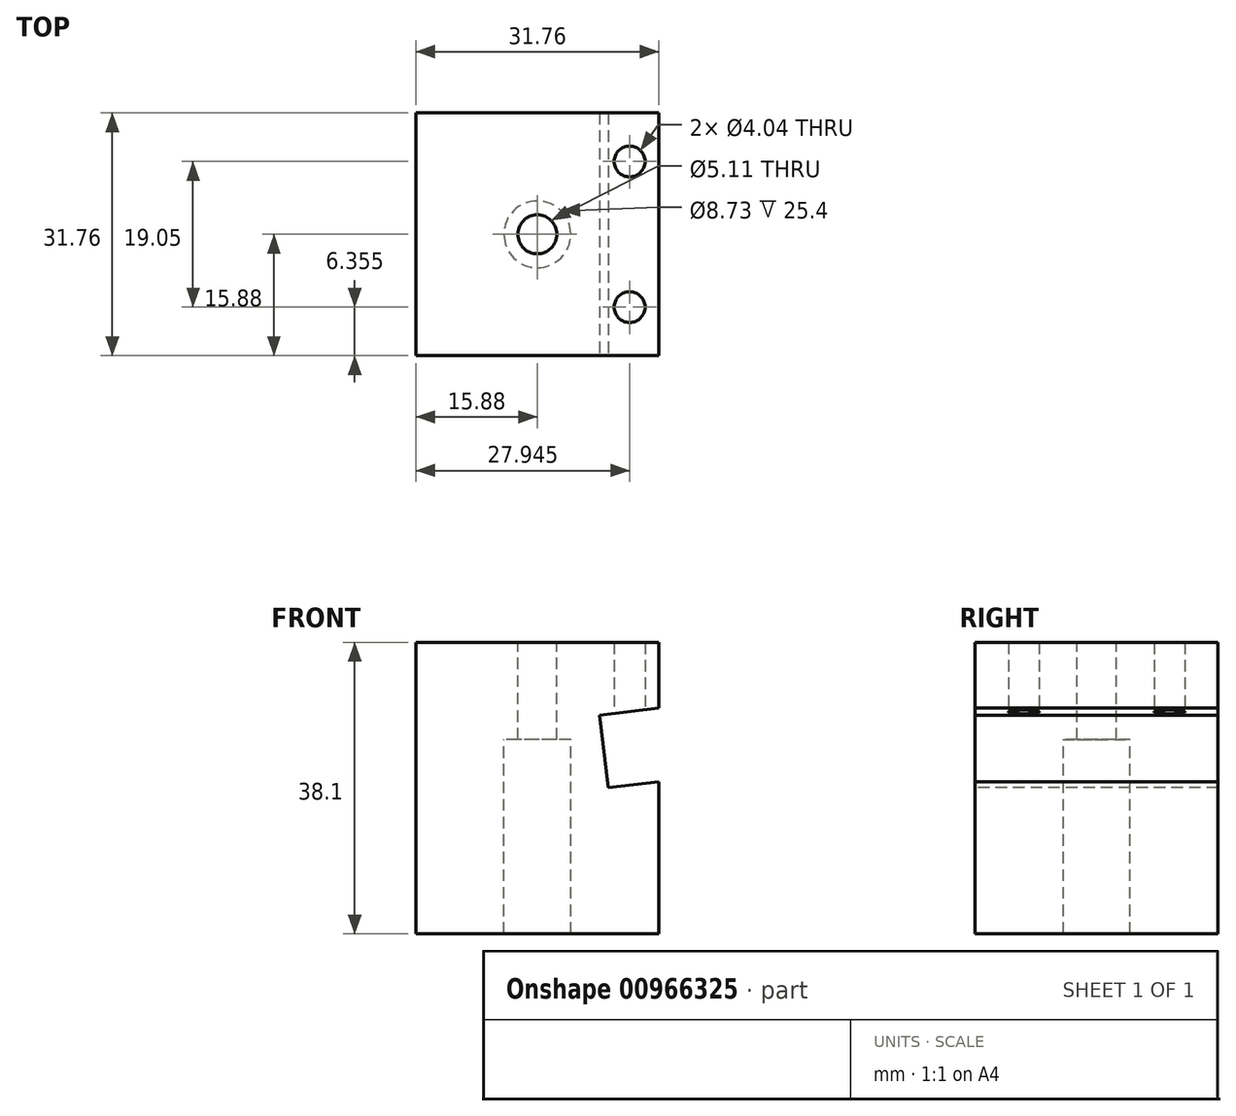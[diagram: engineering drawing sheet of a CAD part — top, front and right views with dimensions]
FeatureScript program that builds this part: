
annotation { "Feature Type Name" : "Feature", "Feature Type Description" : "" }
export const myFeature = defineFeature(function(context is Context, id is Id, definition is map)
    precondition{}
    {
        {
            var Q0;
            Q0=qCreatedBy(makeId("Top.planeOp"),FACE);
            var sketch = newSketch(context, id + "F0", { "sketchPlane" : qUnion([Q0])});
            skLineSegment(sketch, "E0.bottom", {"start": v(15.88, 15.88) * mm, "end": v(-15.88, 15.88) * mm});
            skLineSegment(sketch, "E0.top", {"start": v(15.88, -15.88) * mm, "end": v(-15.88, -15.88) * mm});
            skLineSegment(sketch, "E0.left", {"start": v(15.88, 15.88) * mm, "end": v(15.88, -15.88) * mm});
            skLineSegment(sketch, "E0.right", {"start": v(-15.88, 15.88) * mm, "end": v(-15.88, -15.88) * mm});
            skPoint(sketch, "E0.middle", {"position": v(0, 0) * mm});
            skSolve(sketch);
        }
        {
            var Q0;
            Q0=qSketchRegion(id+"F0",true);
            extrude(context, id + "F1", {"entities" : qUnion([Q0]), "depth" : 38.1 * mm, "offsetDistance" : 25.4 * mm});
        }
        {
            var Q0;
            Q0=qCreatedBy(makeId("Top.planeOp"),FACE);
            var sketch = newSketch(context, id + "F2", { "sketchPlane" : qUnion([Q0])});
            skPoint(sketch, "E1", {"position": v(0, 0) * mm});
            skSolve(sketch);
        }
        {
            var Q0;
            Q0=sQuery(id+"F2.wireOp",VERTEX,"E1");
            var Q1;
            Q1=makeQuery(id+"F1.opExtrude","SWEPT_BODY",BODY,{"disambiguationData":[OSD([sQuery(id+"F0.wireOp",EDGE,"E0.bottom"),sQuery(id+"F0.wireOp",EDGE,"E0.top"),sQuery(id+"F0.wireOp",EDGE,"E0.left"),sQuery(id+"F0.wireOp",EDGE,"E0.right")])]});
            hole(context, id + "F3", {"style" : HoleStyle.C_BORE, "endStyle" : HoleEndStyle.THROUGH, "oppositeDirection" : true, "standardTappedOrClearance" : lookupTablePath({ "standard" : "ANSI", "size" : "#7 (0.2)", "type" : "Drilled" }), "standardBlindInLast" : lookupTablePath({ "standard" : "ANSI", "size" : "#7", "type" : "Drilled" }), "holeDiameter" : 5.1 * mm, "cBoreDiameter" : 8.73 * mm, "cBoreDepth" : 25.4 * mm, "isTappedThrough" : true, "tappedDepth" : 18.42 * mm, "tapClearance" : 3, "startFromSketch" : true, "locations" : qUnion([Q0]), "scope" : qUnion([Q1])});
        }
        {
            var Q0;
            Q0=makeQuery(id+"F1.opExtrude","SWEPT_FACE",FACE,{"disambiguationData":[OSD([sQuery(id+"F0.wireOp",EDGE,"E0.top")])]});
            var sketch = newSketch(context, id + "F4", { "sketchPlane" : qUnion([Q0])});
            skLineSegment(sketch, "E2", {"start": v(33.32, 31.63) * mm, "end": v(8.11, 28.54) * mm});
            skLineSegment(sketch, "E3", {"start": v(8.11, 28.54) * mm, "end": v(9.27, 19.09) * mm});
            skLineSegment(sketch, "E4", {"start": v(9.27, 19.09) * mm, "end": v(34.48, 22.18) * mm});
            skLineSegment(sketch, "E5", {"start": v(34.48, 22.18) * mm, "end": v(33.32, 31.63) * mm});
            skLineSegment(sketch, "E6", {"start": v(8.7, 23.81) * mm, "end": v(74.38, 23.81) * mm, "construction": true});
            skSolve(sketch);
        }
        {
            var Q0;
            Q0=qSketchRegion(id+"F4",true);
            extrude(context, id + "F5", {"entities" : qUnion([Q0]), "operationType" : NewBodyOperationType.REMOVE, "endBound" : BoundingType.THROUGH_ALL, "oppositeDirection" : true, "depth" : 25.4 * mm, "offsetDistance" : 25.4 * mm});
        }
        {
            var Q0;
            Q0=makeQuery(id+"F1.opExtrude","CAP_FACE",FACE,{"disambiguationData":[OSD([sQuery(id+"F0.wireOp",EDGE,"E0.bottom"),sQuery(id+"F0.wireOp",EDGE,"E0.top"),sQuery(id+"F0.wireOp",EDGE,"E0.left"),sQuery(id+"F0.wireOp",EDGE,"E0.right")])],"isStart":false});
            var sketch = newSketch(context, id + "F6", { "sketchPlane" : qUnion([Q0])});
            skLineSegment(sketch, "E7", {"start": v(12.07, -9.53) * mm, "end": v(12.07, 9.53) * mm, "construction": true});
            skPoint(sketch, "E8", {"position": v(12.07, 9.53) * mm});
            skPoint(sketch, "E9", {"position": v(12.07, -9.53) * mm});
            skSolve(sketch);
        }
        {
            var Q0;
            Q0=sQuery(id+"F6.wireOp",VERTEX,"E9");
            var Q1;
            Q1=sQuery(id+"F6.wireOp",VERTEX,"E8");
            var Q2;
            Q2=makeQuery(id+"F1.opExtrude","SWEPT_BODY",BODY,{"disambiguationData":[OSD([sQuery(id+"F0.wireOp",EDGE,"E0.bottom"),sQuery(id+"F0.wireOp",EDGE,"E0.top"),sQuery(id+"F0.wireOp",EDGE,"E0.left"),sQuery(id+"F0.wireOp",EDGE,"E0.right")])]});
            hole(context, id + "F7", {"style" : HoleStyle.SIMPLE, "endStyle" : HoleEndStyle.BLIND, "standardTappedOrClearance" : lookupTablePath({ "standard" : "ANSI", "engagement" : "75%", "pitch" : "32 tpi", "size" : "#10", "type" : "Tapped" }), "standardBlindInLast" : lookupTablePath({ "standard" : "ANSI", "engagement" : "75%", "pitch" : "32 tpi", "size" : "#10", "type" : "Tapped" }), "holeDiameter" : 4.04 * mm, "showTappedDepth" : true, "holeDepth" : 9.5 * mm, "isTappedThrough" : true, "tappedDepth" : 7.11 * mm, "tapClearance" : 3, "startFromSketch" : true, "locations" : qUnion([Q0, Q1]), "scope" : qUnion([Q2]), "majorDiameter" : 4.83 * mm});
        }
    });
